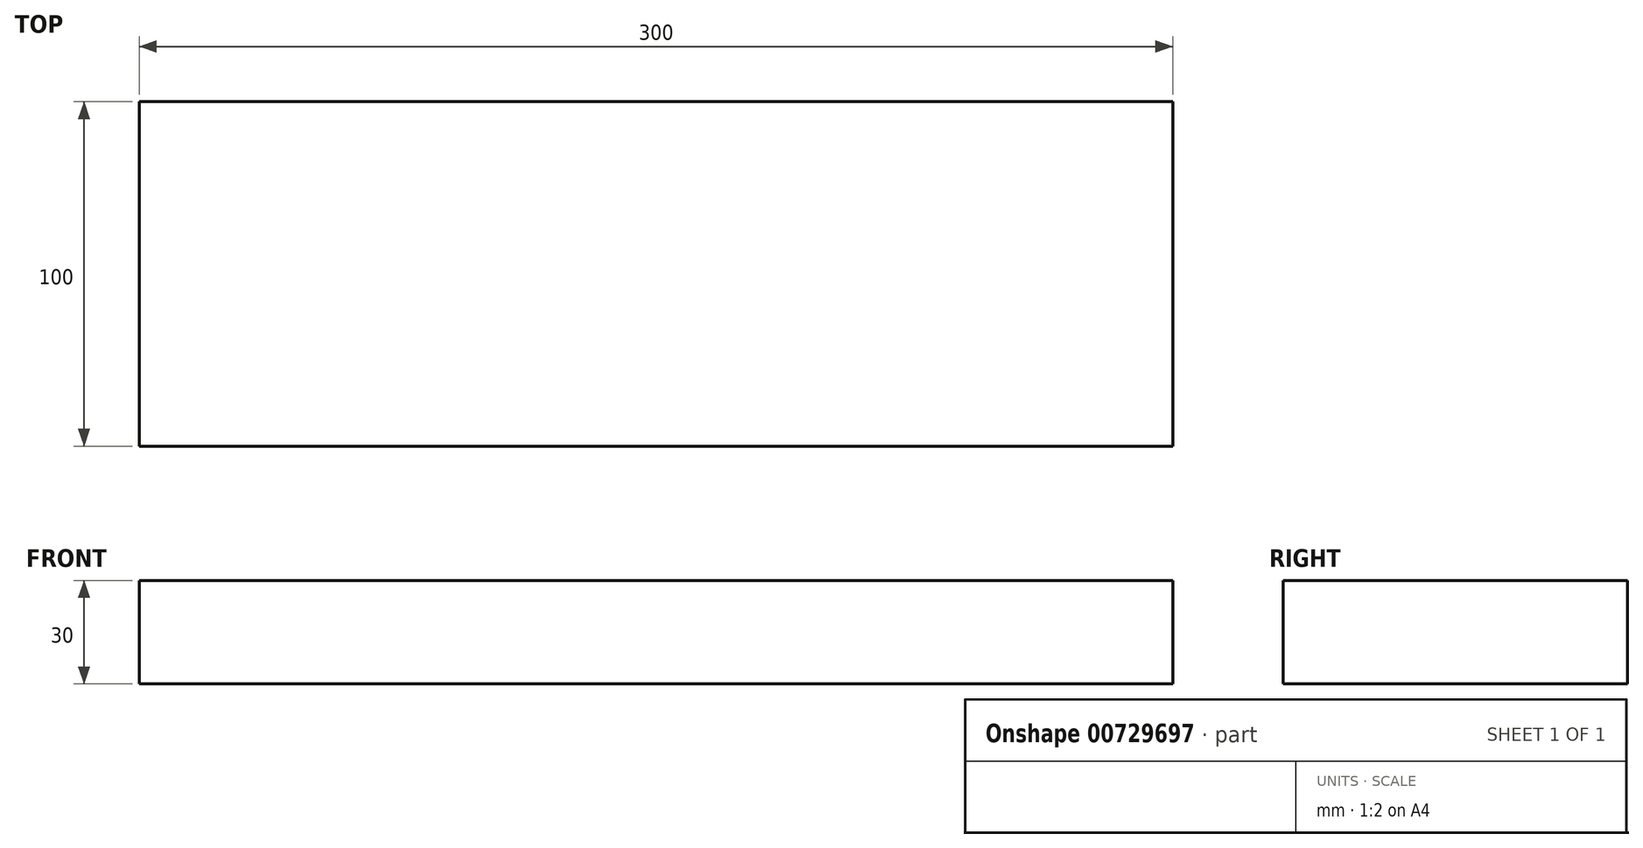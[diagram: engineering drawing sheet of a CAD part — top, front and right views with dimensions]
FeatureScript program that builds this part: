
annotation { "Feature Type Name" : "Feature", "Feature Type Description" : "" }
export const myFeature = defineFeature(function(context is Context, id is Id, definition is map)
    precondition{}
    {
        {
            var Q0;
            Q0=qCreatedBy(makeId("Top.planeOp"),FACE);
            var sketch = newSketch(context, id + "F0", { "sketchPlane" : qUnion([Q0])});
            skLineSegment(sketch, "E0.bottom", {"start": v(-183.01, -59.87) * mm, "end": v(116.99, -59.87) * mm});
            skLineSegment(sketch, "E0.top", {"start": v(-183.01, -159.87) * mm, "end": v(116.99, -159.87) * mm});
            skLineSegment(sketch, "E0.left", {"start": v(-183.01, -59.87) * mm, "end": v(-183.01, -159.87) * mm});
            skLineSegment(sketch, "E0.right", {"start": v(116.99, -59.87) * mm, "end": v(116.99, -159.87) * mm});
            skSolve(sketch);
        }
        {
            var Q0;
            Q0 = qSketchRegion(id + "F0", true);
            extrude(context, id + "F1", {"entities" : qUnion([Q0]), "depth" : 30 * mm, "offsetDistance" : 25 * mm});
        }
    });
